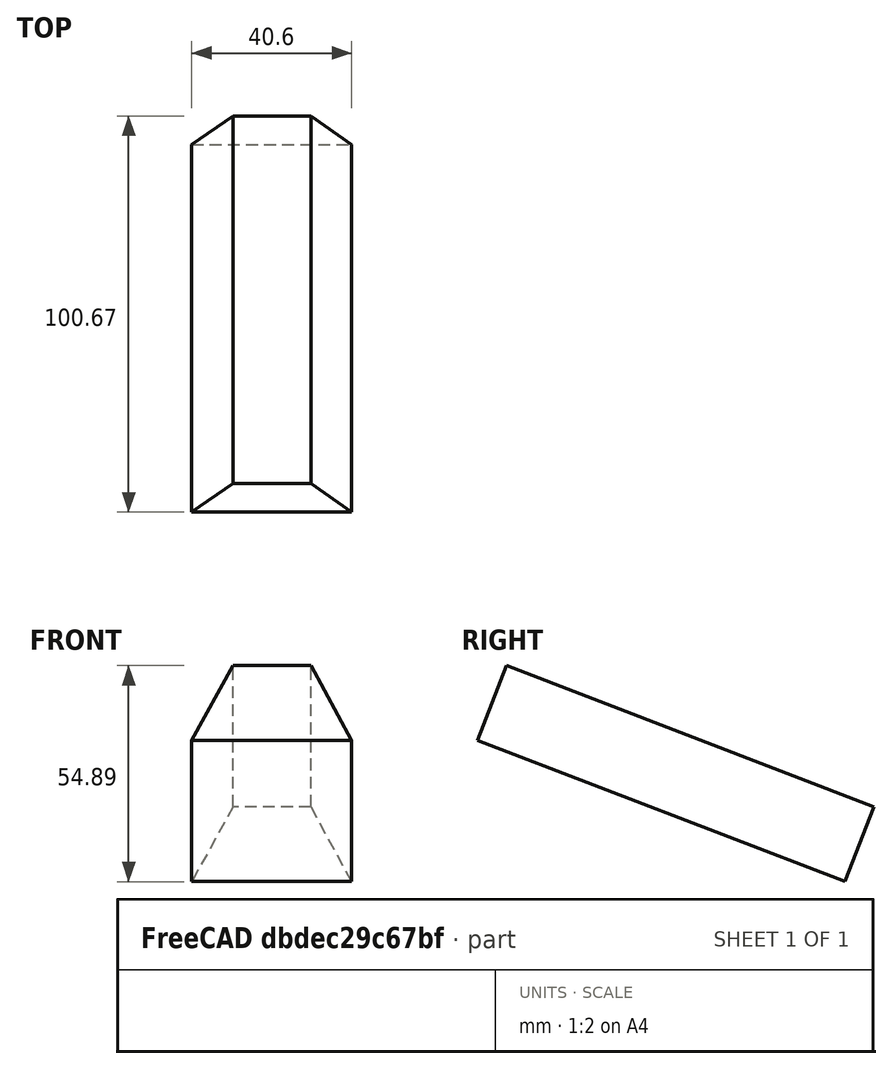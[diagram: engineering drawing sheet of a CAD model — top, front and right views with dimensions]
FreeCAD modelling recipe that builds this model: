
FCSTD DOCUMENT  (FreeCAD 0.21R33694 (Git))
Label: OJT1_T16R01_trapezi
License: All rights reserved
LicenseURL: http://en.wikipedia.org/wiki/All_rights_reserved
objects: Sketcher::SketchObject×1, PartDesign::Pad×1, PartDesign::Body×1
note: 4 computed .brp shape members not serialized (recipe doc carries the construction recipe); baked Part::Feature solids carry a one-line shape summary decoded from their .brp

FEATURE [Sketcher::SketchObject] Sketch
  FullyConstrained = false
  MapMode = 5
  Support = -> [XY_Plane]
  sketch-geometry (4):
    g0: LineSegment StartX=-9.89899 StartY=29.3939 StartZ=0 EndX=-20.404 EndY=8.9899 EndZ=0
    g1: LineSegment StartX=-20.404 StartY=8.9899 StartZ=0 EndX=20.202 EndY=8.9899 EndZ=0
    g2: LineSegment StartX=20.202 StartY=8.9899 StartZ=0 EndX=9.89898 EndY=29.3939 EndZ=0
    g3: LineSegment StartX=9.89898 StartY=29.3939 StartZ=0 EndX=-9.89899 EndY=29.3939 EndZ=0
  constraints (6):
    c: Coincident(g0,g1)
    c: Horizontal(g1)
    c: Coincident(g1,g2)
    c: Coincident(g2,g3)
    c: Coincident(g3,g0)
    c: Horizontal(g3)
FEATURE [PartDesign::Pad] Pad
  Direction = (0,0,1)
  Length = 100
  Length2 = 10
  Profile = -> Sketch
  ReferenceAxis = -> Sketch [N_Axis]
  Type = 0
FEATURE [PartDesign::Body] Body
  Group = -> [Sketch,Pad]
  Origin = -> Origin
  Placement = pos=(0,0,0) rot=(1,0,0;1.20428rad)
  Tip = -> Pad
